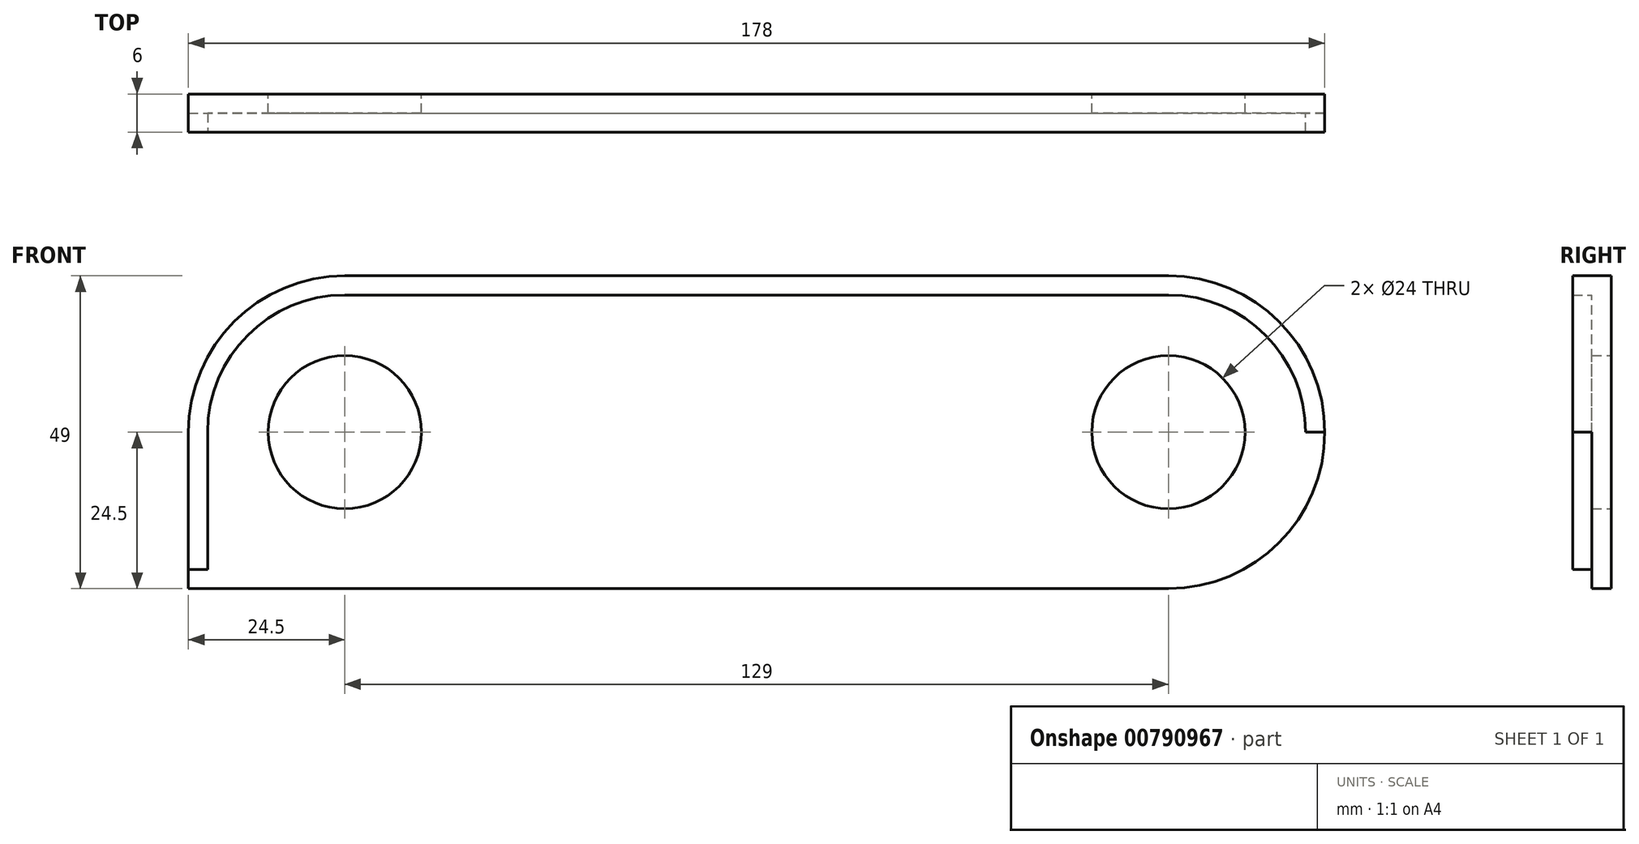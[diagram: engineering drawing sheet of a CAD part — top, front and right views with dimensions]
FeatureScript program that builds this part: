
annotation { "Feature Type Name" : "Feature", "Feature Type Description" : "" }
export const myFeature = defineFeature(function(context is Context, id is Id, definition is map)
    precondition{}
    {
        {
            var Q0;
            Q0=qCreatedBy(makeId("Front.planeOp"),FACE);
            var sketch = newSketch(context, id + "F0", { "sketchPlane" : qUnion([Q0])});
            skLineSegment(sketch, "E0.bottom", {"start": v(64.5, 22.5) * mm, "end": v(-64.5, 22.5) * mm, "construction": true});
            skLineSegment(sketch, "E0.top", {"start": v(64.5, -22.5) * mm, "end": v(-64.5, -22.5) * mm, "construction": true});
            skLineSegment(sketch, "E0.left", {"start": v(64.5, 22.5) * mm, "end": v(64.5, -22.5) * mm, "construction": true});
            skLineSegment(sketch, "E0.right", {"start": v(-64.5, 22.5) * mm, "end": v(-64.5, -22.5) * mm, "construction": true});
            skPoint(sketch, "E0.middle", {"position": v(0, 0) * mm});
            skArc(sketch, "E1", {"start": v(64.5, -22.5) * mm, "mid": v(87, 0) * mm, "end": v(64.5, 22.5) * mm, "construction": true});
            skArc(sketch, "E2", {"start": v(-64.5, 22.5) * mm, "mid": v(-87, 0) * mm, "end": v(-64.5, -22.5) * mm, "construction": true});
            skLineSegment(sketch, "E3", {"start": v(-64.5, 0) * mm, "end": v(-87, 0) * mm, "construction": true});
            skLineSegment(sketch, "E4", {"start": v(-87, 0) * mm, "end": v(-87, -22.5) * mm, "construction": true});
            skLineSegment(sketch, "E5", {"start": v(-87, -22.5) * mm, "end": v(-64.5, -22.5) * mm, "construction": true});
            skLineSegment(sketch, "E6.bottom", {"start": v(64.5, 24.5) * mm, "end": v(-64.5, 24.5) * mm});
            skLineSegment(sketch, "E6.top", {"start": v(64.5, -24.5) * mm, "end": v(-64.5, -24.5) * mm});
            skArc(sketch, "E7", {"start": v(-64.5, 24.5) * mm, "mid": v(-89, 0) * mm, "end": v(-64.5, -24.5) * mm});
            skArc(sketch, "E8", {"start": v(64.5, -24.5) * mm, "mid": v(89, 0) * mm, "end": v(64.5, 24.5) * mm});
            skCircle(sketch, "E9", {"center": v(-64.5, 0) * mm, "radius": 12 * mm});
            skCircle(sketch, "E10", {"center": v(64.5, 0) * mm, "radius": 12 * mm});
            skLineSegment(sketch, "E11", {"start": v(-89, 0) * mm, "end": v(-89, -24.5) * mm});
            skLineSegment(sketch, "E12", {"start": v(-89, -24.5) * mm, "end": v(-64.5, -24.5) * mm});
            skSolve(sketch);
        }
        {
            var Q0;
            Q0 = qSketchRegion(id + "F0", true);
            extrude(context, id + "F1", {"entities" : qUnion([Q0]), "depth" : 3 * mm, "offsetDistance" : 25 * mm});
        }
        {
            var Q0;
            Q0=makeQuery(id+"F1.opExtrude","CAP_FACE",FACE,{"disambiguationData":[OSD([sQuery(id+"F0.wireOp",EDGE,"E6.bottom"),sQuery(id+"F0.wireOp",EDGE,"E6.top"),sQuery(id+"F0.wireOp",EDGE,"E7"),sQuery(id+"F0.wireOp",EDGE,"E8"),sQuery(id+"F0.wireOp",EDGE,"E9"),sQuery(id+"F0.wireOp",EDGE,"E10"),sQuery(id+"F0.wireOp",EDGE,"E11"),sQuery(id+"F0.wireOp",EDGE,"E12")])],"isStart":false});
            var sketch = newSketch(context, id + "F2", { "sketchPlane" : qUnion([Q0])});
            skLineSegment(sketch, "E13", {"start": v(-89, -24.5) * mm, "end": v(-89, 0) * mm});
            skLineSegment(sketch, "E14", {"start": v(-64.5, 24.5) * mm, "end": v(64.5, 24.5) * mm});
            skArc(sketch, "E15", {"start": v(-64.5, 24.5) * mm, "mid": v(-81.82, 17.32) * mm, "end": v(-89, 0) * mm});
            skLineSegment(sketch, "E16", {"start": v(-86, -24.5) * mm, "end": v(-86, 0) * mm});
            skLineSegment(sketch, "E17", {"start": v(-64.5, 21.5) * mm, "end": v(64.5, 21.5) * mm});
            skArc(sketch, "E18", {"start": v(-64.5, 21.5) * mm, "mid": v(-79.7, 15.2) * mm, "end": v(-86, 0) * mm});
            skArc(sketch, "E19", {"start": v(89, 0) * mm, "mid": v(81.82, 17.32) * mm, "end": v(64.5, 24.5) * mm});
            skLineSegment(sketch, "E20", {"start": v(89, 0) * mm, "end": v(86, 0) * mm});
            skArc(sketch, "E21", {"start": v(86, 0) * mm, "mid": v(79.7, 15.2) * mm, "end": v(64.5, 21.5) * mm});
            skLineSegment(sketch, "E22", {"start": v(-89, -24.5) * mm, "end": v(-86, -24.5) * mm});
            skSolve(sketch);
        }
        {
            var Q0;
            Q0 = qSketchRegion(id + "F2", true);
            extrude(context, id + "F3", {"entities" : qUnion([Q0]), "operationType" : NewBodyOperationType.ADD, "depth" : 3 * mm, "offsetDistance" : 25 * mm});
        }
        {
            var Q0;
            Q0=makeQuery(id+"F3.opExtrude","CAP_FACE",FACE,{"disambiguationData":[OSD([sQuery(id+"F2.wireOp",EDGE,"E13"),sQuery(id+"F2.wireOp",EDGE,"E14"),sQuery(id+"F2.wireOp",EDGE,"E15"),sQuery(id+"F2.wireOp",EDGE,"E16"),sQuery(id+"F2.wireOp",EDGE,"E17"),sQuery(id+"F2.wireOp",EDGE,"E18"),sQuery(id+"F2.wireOp",EDGE,"E19"),sQuery(id+"F2.wireOp",EDGE,"E20"),sQuery(id+"F2.wireOp",EDGE,"E21"),sQuery(id+"F2.wireOp",EDGE,"E22")])],"isStart":false});
            var sketch = newSketch(context, id + "F4", { "sketchPlane" : qUnion([Q0])});
            skLineSegment(sketch, "E23.bottom", {"start": v(-89, -24.5) * mm, "end": v(-86, -24.5) * mm});
            skLineSegment(sketch, "E23.top", {"start": v(-89, -21.5) * mm, "end": v(-86, -21.5) * mm});
            skLineSegment(sketch, "E23.left", {"start": v(-89, -24.5) * mm, "end": v(-89, -21.5) * mm});
            skLineSegment(sketch, "E23.right", {"start": v(-86, -24.5) * mm, "end": v(-86, -21.5) * mm});
            skSolve(sketch);
        }
        {
            var Q0;
            Q0 = qSketchRegion(id + "F4", true);
            extrude(context, id + "F5", {"entities" : qUnion([Q0]), "operationType" : NewBodyOperationType.REMOVE, "oppositeDirection" : true, "depth" : 3 * mm, "offsetDistance" : 25 * mm});
        }
    });
